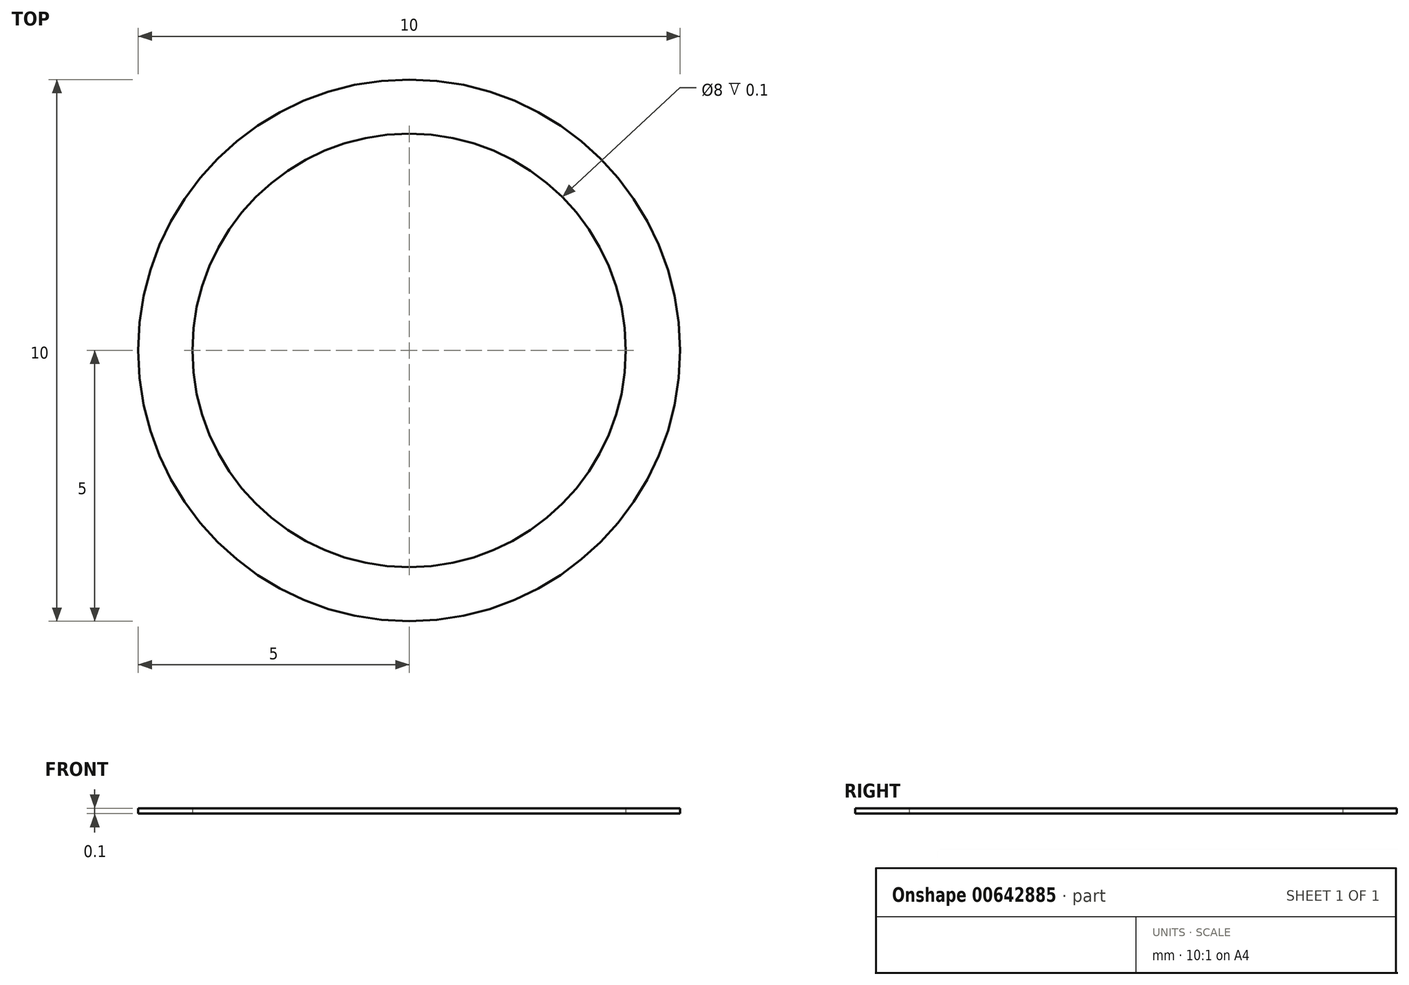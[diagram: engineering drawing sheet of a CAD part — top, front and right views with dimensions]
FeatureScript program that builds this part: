
annotation { "Feature Type Name" : "Feature", "Feature Type Description" : "" }
export const myFeature = defineFeature(function(context is Context, id is Id, definition is map)
    precondition{}
    {
        {
            var Q0;
            Q0=qCreatedBy(makeId("Top.planeOp"),FACE);
            var sketch = newSketch(context, id + "F0", { "sketchPlane" : qUnion([Q0])});
            skCircle(sketch, "E0", {"center": v(0, 0) * mm, "radius": 4 * mm});
            skCircle(sketch, "E1", {"center": v(0, 0) * mm, "radius": 5 * mm});
            skSolve(sketch);
        }
        {
            var Q0;
            Q0=makeQuery(id+"F0.imprint","IMPRINT",FACE,{"disambiguationData":[TD([[makeQuery(id+"F0.imprint","IMPRINT",EDGE,{"derivedFrom":sQuery(id+"F0.wireOp",EDGE,"E0")}),-1.0]])]});
            extrude(context, id + "F1", {"entities" : qUnion([Q0]), "depth" : .1 * mm, "offsetDistance" : 25 * mm});
        }
        {
            var Q0;
            Q0=qCreatedBy(makeId("Top.planeOp"),FACE);
            cPlane(context, id + "F2", {"entities" : qUnion([Q0]), "cplaneType" : CPlaneType.OFFSET, "offset" : (17 + 7) * mm, "width" : 150 * mm, "height" : 150 * mm});
        }
    });
